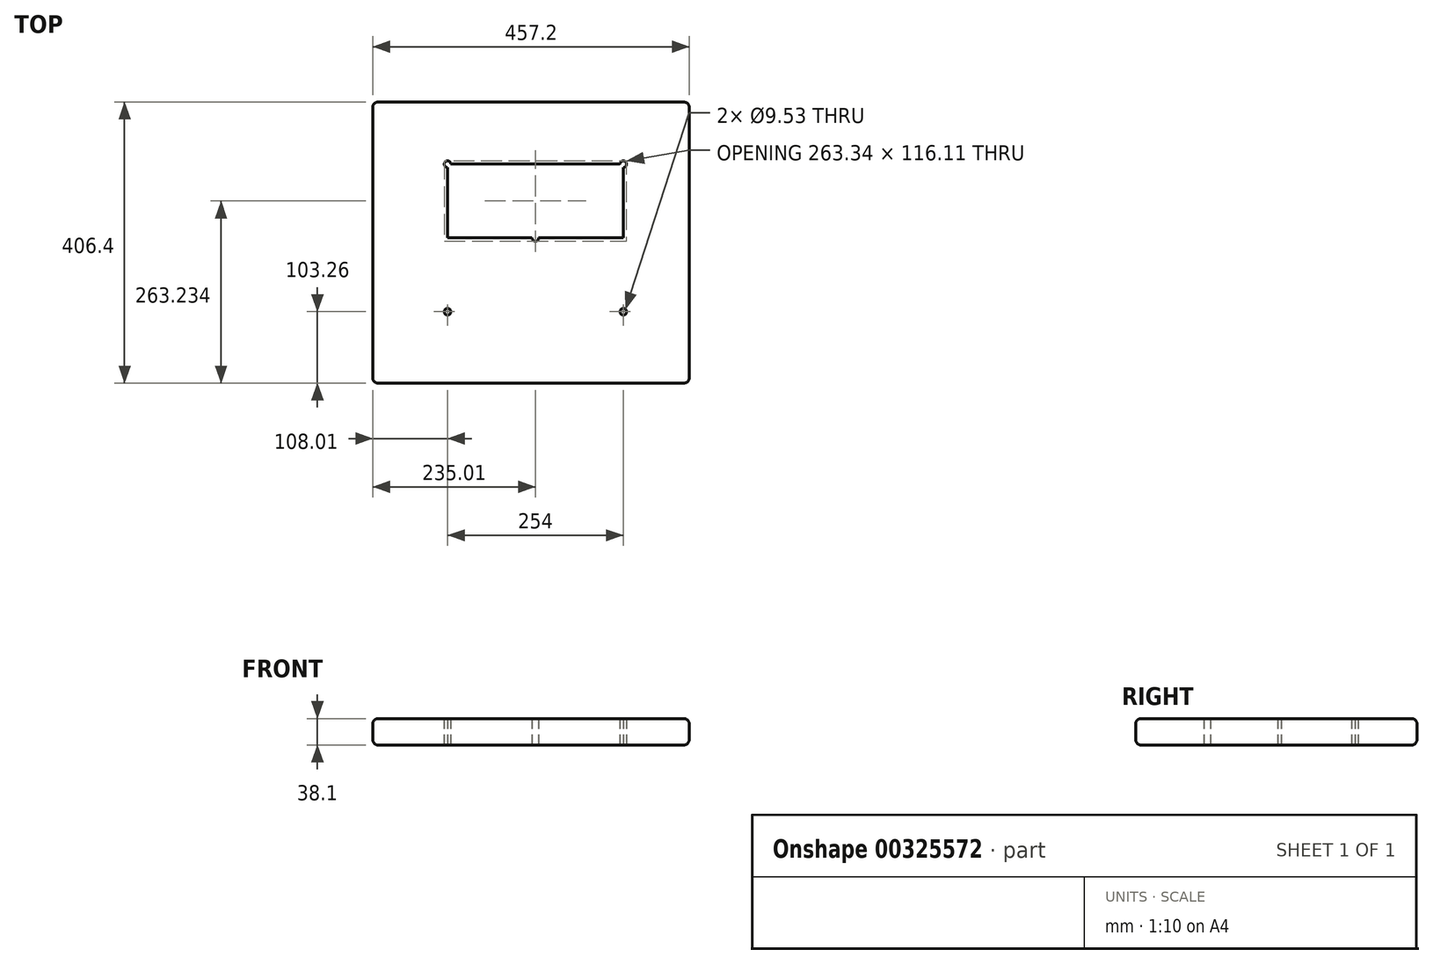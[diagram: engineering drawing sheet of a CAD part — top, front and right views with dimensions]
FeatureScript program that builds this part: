
annotation { "Feature Type Name" : "Feature", "Feature Type Description" : "" }
export const myFeature = defineFeature(function(context is Context, id is Id, definition is map)
    precondition{}
    {
        {
            var Q0;
            Q0=qCreatedBy(makeId("Top.planeOp"),FACE);
            var sketch = newSketch(context, id + "F0", { "sketchPlane" : qUnion([Q0])});
            skLineSegment(sketch, "E0.bottom", {"start": v(-235, 196.46) * mm, "end": v(222.2, 196.46) * mm});
            skLineSegment(sketch, "E0.top", {"start": v(-235, -209.94) * mm, "end": v(222.2, -209.94) * mm});
            skLineSegment(sketch, "E0.left", {"start": v(-235, 196.46) * mm, "end": v(-235, -209.94) * mm});
            skLineSegment(sketch, "E0.right", {"start": v(222.2, 196.46) * mm, "end": v(222.2, -209.94) * mm});
            skPoint(sketch, "E1", {"position": v(-6.4, -209.94) * mm});
            skPoint(sketch, "E2", {"position": v(222.2, -6.74) * mm});
            skPoint(sketch, "E3.start.orphan", {"position": v(-268.88, 0) * mm});
            skCircle(sketch, "E4", {"center": v(0, 0) * mm, "radius": 4.76 * mm});
            skLineSegment(sketch, "E5", {"start": v(-127, 259.43) * mm, "end": v(-127, -231.27) * mm});
            skLineSegment(sketch, "E6", {"start": v(0, 267.18) * mm, "end": v(0, -251.57) * mm});
            skLineSegment(sketch, "E7", {"start": v(127, 261.27) * mm, "end": v(127, -243.45) * mm});
            skLineSegment(sketch, "E8", {"start": v(-268.88, 0) * mm, "end": v(282.24, 0) * mm});
            skLineSegment(sketch, "E9", {"start": v(-273.4, 106.68) * mm, "end": v(267.11, 106.68) * mm});
            skLineSegment(sketch, "E10", {"start": v(-266.98, -106.68) * mm, "end": v(260.7, -106.68) * mm});
            skCircle(sketch, "E11", {"center": v(-127, 106.68) * mm, "radius": 4.76 * mm});
            skCircle(sketch, "E12", {"center": v(127, 106.68) * mm, "radius": 4.76 * mm});
            skCircle(sketch, "E13", {"center": v(127, -106.68) * mm, "radius": 4.76 * mm});
            skCircle(sketch, "E14", {"center": v(-127, -106.68) * mm, "radius": 4.76 * mm});
            skSolve(sketch);
        }
        {
            var Q0;
            {var subQ1=sQuery(id+"F0.wireOp",EDGE,"E0.top");var subQ6=sQuery(id+"F0.wireOp",EDGE,"E0.left");var subQ9=makeQuery(id+"F0.imprint","INTERSECT",VERTEX,{"derivedFrom":[subQ1,subQ6]});Q0=makeQuery(id+"F0.imprint","IMPRINT",FACE,{"disambiguationData":[TD([[makeQuery(id+"F0.imprint","IMPRINT",EDGE,{"disambiguationData":[TD([[subQ9,-1.0]])],"derivedFrom":subQ1}),1.0]])]});}
            var Q1;
            {var subQ5=sQuery(id+"F0.wireOp",EDGE,"E0.top");var subQ7=sQuery(id+"F0.wireOp",EDGE,"E5");var subQ8=makeQuery(id+"F0.imprint","INTERSECT",VERTEX,{"derivedFrom":[subQ5,subQ7]});Q1=makeQuery(id+"F0.imprint","IMPRINT",FACE,{"disambiguationData":[TD([[makeQuery(id+"F0.imprint","IMPRINT",EDGE,{"disambiguationData":[TD([[subQ8,-1.0]])],"derivedFrom":subQ5}),1.0]])]});}
            var Q2;
            {var subQ1=sQuery(id+"F0.wireOp",EDGE,"E4");var subQ5=sQuery(id+"F0.wireOp",EDGE,"E8");var subQ6=makeQuery(id+"F0.imprint","INTERSECT",VERTEX,{"disambiguationData":[OD(1.0)],"derivedFrom":[subQ1,subQ5]});Q2=makeQuery(id+"F0.imprint","IMPRINT",FACE,{"disambiguationData":[TD([[makeQuery(id+"F0.imprint","IMPRINT",EDGE,{"disambiguationData":[TD([[subQ6,-1.0]])],"derivedFrom":subQ1}),-1.0]])]});}
            var Q3;
            {var subQ1=sQuery(id+"F0.wireOp",EDGE,"E0.left");var subQ5=sQuery(id+"F0.wireOp",EDGE,"E8");var subQ6=makeQuery(id+"F0.imprint","INTERSECT",VERTEX,{"derivedFrom":[subQ1,subQ5]});Q3=makeQuery(id+"F0.imprint","IMPRINT",FACE,{"disambiguationData":[TD([[makeQuery(id+"F0.imprint","IMPRINT",EDGE,{"disambiguationData":[TD([[subQ6,-1.0]])],"derivedFrom":subQ1}),1.0]])]});}
            var Q4;
            {var subQ1=sQuery(id+"F0.wireOp",EDGE,"E0.left");var subQ5=sQuery(id+"F0.wireOp",EDGE,"E9");var subQ6=makeQuery(id+"F0.imprint","INTERSECT",VERTEX,{"derivedFrom":[subQ1,subQ5]});Q4=makeQuery(id+"F0.imprint","IMPRINT",FACE,{"disambiguationData":[TD([[makeQuery(id+"F0.imprint","IMPRINT",EDGE,{"disambiguationData":[TD([[subQ6,-1.0]])],"derivedFrom":subQ1}),1.0]])]});}
            var Q5;
            {var subQ0=sQuery(id+"F0.wireOp",EDGE,"E6");var subQ1=sQuery(id+"F0.wireOp",EDGE,"E4");var subQ2=makeQuery(id+"F0.imprint","INTERSECT",VERTEX,{"disambiguationData":[OD(0.0)],"derivedFrom":[subQ1,subQ0]});Q5=makeQuery(id+"F0.imprint","IMPRINT",FACE,{"disambiguationData":[TD([[makeQuery(id+"F0.imprint","IMPRINT",EDGE,{"disambiguationData":[TD([[subQ2,-1.0]])],"derivedFrom":subQ1}),-1.0]])]});}
            var Q6;
            {var subQ1=sQuery(id+"F0.wireOp",EDGE,"E0.bottom");var subQ5=sQuery(id+"F0.wireOp",EDGE,"E5");var subQ6=makeQuery(id+"F0.imprint","INTERSECT",VERTEX,{"derivedFrom":[subQ1,subQ5]});Q6=makeQuery(id+"F0.imprint","IMPRINT",FACE,{"disambiguationData":[TD([[makeQuery(id+"F0.imprint","IMPRINT",EDGE,{"disambiguationData":[TD([[subQ6,-1.0]])],"derivedFrom":subQ1}),-1.0]])]});}
            var Q7;
            {var subQ1=sQuery(id+"F0.wireOp",EDGE,"E0.left");var subQ5=sQuery(id+"F0.wireOp",EDGE,"E0.bottom");var subQ6=makeQuery(id+"F0.imprint","INTERSECT",VERTEX,{"derivedFrom":[subQ5,subQ1]});Q7=makeQuery(id+"F0.imprint","IMPRINT",FACE,{"disambiguationData":[TD([[makeQuery(id+"F0.imprint","IMPRINT",EDGE,{"disambiguationData":[TD([[subQ6,-1.0]])],"derivedFrom":subQ5}),-1.0]])]});}
            var Q8;
            {var subQ1=sQuery(id+"F0.wireOp",EDGE,"E0.right");var subQ6=sQuery(id+"F0.wireOp",EDGE,"E0.bottom");var subQ9=makeQuery(id+"F0.imprint","INTERSECT",VERTEX,{"derivedFrom":[subQ6,subQ1]});Q8=makeQuery(id+"F0.imprint","IMPRINT",FACE,{"disambiguationData":[TD([[makeQuery(id+"F0.imprint","IMPRINT",EDGE,{"disambiguationData":[TD([[subQ9,1.0]])],"derivedFrom":subQ6}),-1.0]])]});}
            var Q9;
            {var subQ1=sQuery(id+"F0.wireOp",EDGE,"E0.bottom");var subQ5=sQuery(id+"F0.wireOp",EDGE,"E6");var subQ6=makeQuery(id+"F0.imprint","INTERSECT",VERTEX,{"derivedFrom":[subQ1,subQ5]});Q9=makeQuery(id+"F0.imprint","IMPRINT",FACE,{"disambiguationData":[TD([[makeQuery(id+"F0.imprint","IMPRINT",EDGE,{"disambiguationData":[TD([[subQ6,-1.0]])],"derivedFrom":subQ1}),-1.0]])]});}
            var Q10;
            {var subQ7=sQuery(id+"F0.wireOp",EDGE,"E6");var subQ8=sQuery(id+"F0.wireOp",EDGE,"E4");var subQ9=makeQuery(id+"F0.imprint","INTERSECT",VERTEX,{"disambiguationData":[OD(0.0)],"derivedFrom":[subQ8,subQ7]});Q10=makeQuery(id+"F0.imprint","IMPRINT",FACE,{"disambiguationData":[TD([[makeQuery(id+"F0.imprint","IMPRINT",EDGE,{"disambiguationData":[TD([[subQ9,1.0]])],"derivedFrom":subQ8}),-1.0]])]});}
            var Q11;
            {var subQ0=sQuery(id+"F0.wireOp",EDGE,"E9");var subQ1=sQuery(id+"F0.wireOp",EDGE,"E0.right");var subQ2=makeQuery(id+"F0.imprint","INTERSECT",VERTEX,{"derivedFrom":[subQ1,subQ0]});Q11=makeQuery(id+"F0.imprint","IMPRINT",FACE,{"disambiguationData":[TD([[makeQuery(id+"F0.imprint","IMPRINT",EDGE,{"disambiguationData":[TD([[subQ2,-1.0]])],"derivedFrom":subQ1}),-1.0]])]});}
            var Q12;
            {var subQ0=sQuery(id+"F0.wireOp",EDGE,"E8");var subQ1=sQuery(id+"F0.wireOp",EDGE,"E4");var subQ2=makeQuery(id+"F0.imprint","INTERSECT",VERTEX,{"disambiguationData":[OD(0.0)],"derivedFrom":[subQ1,subQ0]});Q12=makeQuery(id+"F0.imprint","IMPRINT",FACE,{"disambiguationData":[TD([[makeQuery(id+"F0.imprint","IMPRINT",EDGE,{"disambiguationData":[TD([[subQ2,1.0]])],"derivedFrom":subQ1}),-1.0]])]});}
            var Q13;
            {var subQ0=sQuery(id+"F0.wireOp",EDGE,"E8");var subQ1=sQuery(id+"F0.wireOp",EDGE,"E0.right");var subQ2=makeQuery(id+"F0.imprint","INTERSECT",VERTEX,{"derivedFrom":[subQ1,subQ0]});Q13=makeQuery(id+"F0.imprint","IMPRINT",FACE,{"disambiguationData":[TD([[makeQuery(id+"F0.imprint","IMPRINT",EDGE,{"disambiguationData":[TD([[subQ2,-1.0]])],"derivedFrom":subQ1}),-1.0]])]});}
            var Q14;
            {var subQ1=sQuery(id+"F0.wireOp",EDGE,"E6");var subQ5=sQuery(id+"F0.wireOp",EDGE,"E0.top");var subQ6=makeQuery(id+"F0.imprint","INTERSECT",VERTEX,{"derivedFrom":[subQ5,subQ1]});Q14=makeQuery(id+"F0.imprint","IMPRINT",FACE,{"disambiguationData":[TD([[makeQuery(id+"F0.imprint","IMPRINT",EDGE,{"disambiguationData":[TD([[subQ6,-1.0]])],"derivedFrom":subQ5}),1.0]])]});}
            var Q15;
            {var subQ1=sQuery(id+"F0.wireOp",EDGE,"E0.right");var subQ6=sQuery(id+"F0.wireOp",EDGE,"E0.top");var subQ9=makeQuery(id+"F0.imprint","INTERSECT",VERTEX,{"derivedFrom":[subQ6,subQ1]});Q15=makeQuery(id+"F0.imprint","IMPRINT",FACE,{"disambiguationData":[TD([[makeQuery(id+"F0.imprint","IMPRINT",EDGE,{"disambiguationData":[TD([[subQ9,1.0]])],"derivedFrom":subQ6}),1.0]])]});}
            extrude(context, id + "F1", {"entities" : qUnion([Q0, Q1, Q2, Q3, Q4, Q5, Q6, Q7, Q8, Q9, Q10, Q11, Q12, Q13, Q14, Q15]), "depth" : 38.1 * mm});
        }
        {
            var Q0;
            Q0=makeQuery(id+"F1.opExtrude","CAP_EDGE",EDGE,{"disambiguationData":[OSD([sQuery(id+"F0.wireOp",EDGE,"E0.right")])],"isStart":false});
            var Q1;
            Q1=makeQuery(id+"F1.opExtrude","CAP_EDGE",EDGE,{"disambiguationData":[OSD([sQuery(id+"F0.wireOp",EDGE,"E0.right")])],"isStart":true});
            var Q2;
            Q2=makeQuery(id+"F1.opExtrude","CAP_EDGE",EDGE,{"disambiguationData":[OSD([sQuery(id+"F0.wireOp",EDGE,"E0.top")])],"isStart":true});
            var Q3;
            Q3=makeQuery(id+"F1.opExtrude","SWEPT_EDGE",EDGE,{"disambiguationData":[OSD([sQuery(id+"F0.wireOp",EDGE,"E0.top"),sQuery(id+"F0.wireOp",EDGE,"E0.right")])]});
            var Q4;
            Q4=makeQuery(id+"F1.opExtrude","CAP_EDGE",EDGE,{"disambiguationData":[OSD([sQuery(id+"F0.wireOp",EDGE,"E0.top")])],"isStart":false});
            var Q5;
            Q5=makeQuery(id+"F1.opExtrude","CAP_EDGE",EDGE,{"disambiguationData":[OSD([sQuery(id+"F0.wireOp",EDGE,"E0.bottom")])],"isStart":false});
            var Q6;
            Q6=makeQuery(id+"F1.opExtrude","SWEPT_EDGE",EDGE,{"disambiguationData":[OSD([sQuery(id+"F0.wireOp",EDGE,"E0.bottom"),sQuery(id+"F0.wireOp",EDGE,"E0.right")])]});
            var Q7;
            Q7=makeQuery(id+"F1.opExtrude","CAP_EDGE",EDGE,{"disambiguationData":[OSD([sQuery(id+"F0.wireOp",EDGE,"E0.left")])],"isStart":false});
            var Q8;
            Q8=makeQuery(id+"F1.opExtrude","SWEPT_EDGE",EDGE,{"disambiguationData":[OSD([sQuery(id+"F0.wireOp",EDGE,"E0.top"),sQuery(id+"F0.wireOp",EDGE,"E0.left")])]});
            var Q9;
            Q9=makeQuery(id+"F1.opExtrude","CAP_EDGE",EDGE,{"disambiguationData":[OSD([sQuery(id+"F0.wireOp",EDGE,"E0.left")])],"isStart":true});
            var Q10;
            Q10=makeQuery(id+"F1.opExtrude","SWEPT_EDGE",EDGE,{"disambiguationData":[OSD([sQuery(id+"F0.wireOp",EDGE,"E0.bottom"),sQuery(id+"F0.wireOp",EDGE,"E0.left")])]});
            var Q11;
            Q11=makeQuery(id+"F1.opExtrude","CAP_EDGE",EDGE,{"disambiguationData":[OSD([sQuery(id+"F0.wireOp",EDGE,"E0.bottom")])],"isStart":true});
            fillet(context, id + "F2", {"entities" : qUnion([Q0, Q1, Q2, Q3, Q4, Q5, Q6, Q7, Q8, Q9, Q10, Q11]), "radius" : 7.62 * mm, "tangentPropagation" : true, "allowEdgeOverflow" : false});
        }
    });
